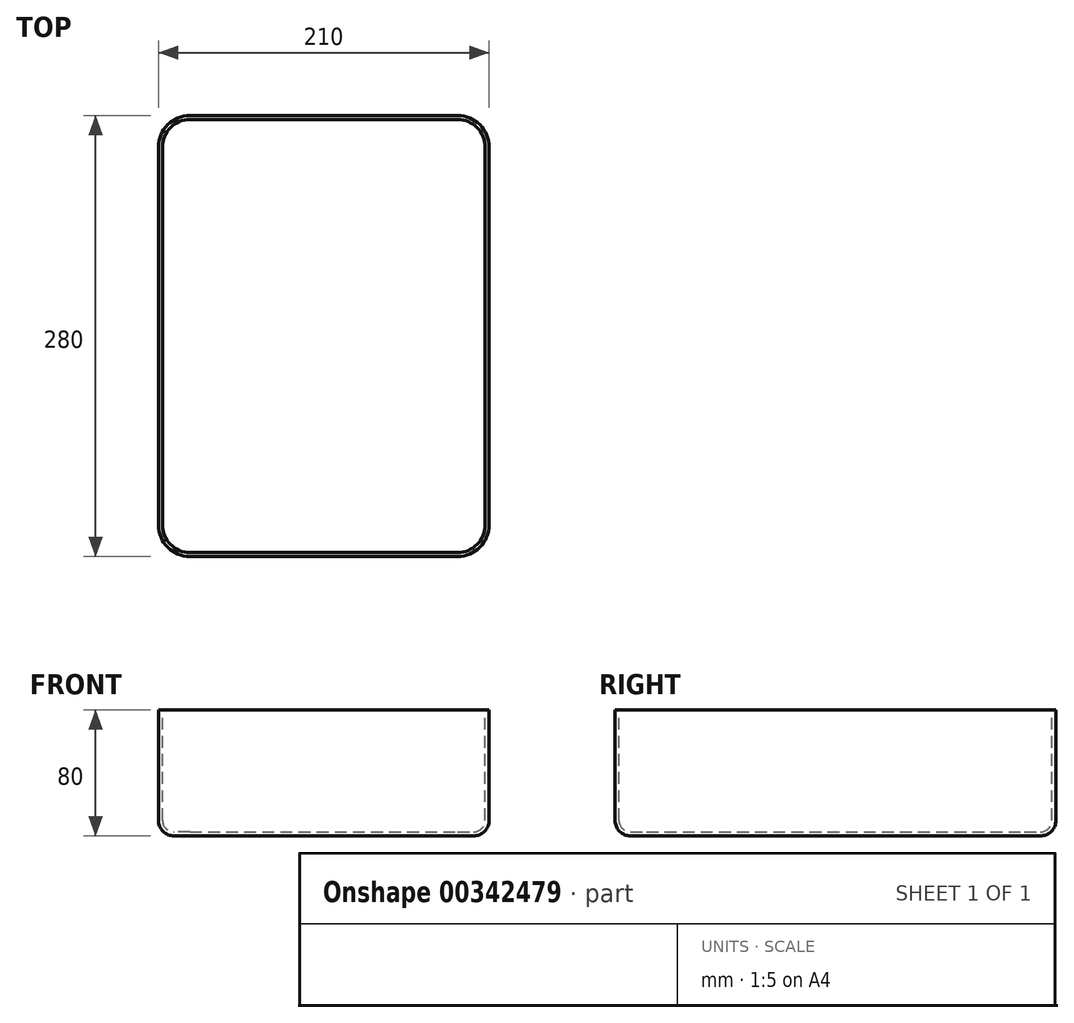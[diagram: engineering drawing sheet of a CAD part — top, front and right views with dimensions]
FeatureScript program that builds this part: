
annotation { "Feature Type Name" : "Feature", "Feature Type Description" : "" }
export const myFeature = defineFeature(function(context is Context, id is Id, definition is map)
    precondition{}
    {
        {
            var Q0;
            Q0=qCreatedBy(makeId("Top.planeOp"),FACE);
            var sketch = newSketch(context, id + "F0", { "sketchPlane" : qUnion([Q0])});
            skLineSegment(sketch, "E0.bottom", {"start": v(0, 0) * mm, "end": v(210, 0) * mm});
            skLineSegment(sketch, "E0.top", {"start": v(0, 280) * mm, "end": v(210, 280) * mm});
            skLineSegment(sketch, "E0.left", {"start": v(0, 0) * mm, "end": v(0, 280) * mm});
            skLineSegment(sketch, "E0.right", {"start": v(210, 0) * mm, "end": v(210, 280) * mm});
            skSolve(sketch);
        }
        {
            var Q0;
            Q0=makeQuery(id+"F0.imprint","IMPRINT",FACE,{"disambiguationData":[TD([[makeQuery(id+"F0.imprint","IMPRINT",EDGE,{"derivedFrom":sQuery(id+"F0.wireOp",EDGE,"E0.bottom")}),1.0]])]});
            extrude(context, id + "F1", {"entities" : qUnion([Q0]), "depth" : 80 * mm});
        }
        {
            var Q0;
            Q0=makeQuery(id+"F1.opExtrude","SWEPT_EDGE",EDGE,{"disambiguationData":[OSD([sQuery(id+"F0.wireOp",EDGE,"E0.top"),sQuery(id+"F0.wireOp",EDGE,"E0.left")])]});
            var Q1;
            Q1=makeQuery(id+"F1.opExtrude","SWEPT_EDGE",EDGE,{"disambiguationData":[OSD([sQuery(id+"F0.wireOp",EDGE,"E0.bottom"),sQuery(id+"F0.wireOp",EDGE,"E0.left")])]});
            var Q2;
            Q2=makeQuery(id+"F1.opExtrude","SWEPT_EDGE",EDGE,{"disambiguationData":[OSD([sQuery(id+"F0.wireOp",EDGE,"E0.bottom"),sQuery(id+"F0.wireOp",EDGE,"E0.right")])]});
            var Q3;
            Q3=makeQuery(id+"F1.opExtrude","SWEPT_EDGE",EDGE,{"disambiguationData":[OSD([sQuery(id+"F0.wireOp",EDGE,"E0.top"),sQuery(id+"F0.wireOp",EDGE,"E0.right")])]});
            fillet(context, id + "F2", {"entities" : qUnion([Q0, Q1, Q2, Q3]), "radius" : 20 * mm, "tangentPropagation" : true, "allowEdgeOverflow" : false});
        }
        {
            var Q0;
            Q0=makeQuery(id+"F1.opExtrude","CAP_EDGE",EDGE,{"disambiguationData":[OSD([sQuery(id+"F0.wireOp",EDGE,"E0.left")])],"isStart":true});
            fillet(context, id + "F3", {"entities" : qUnion([Q0]), "radius" : 10 * mm, "tangentPropagation" : true, "allowEdgeOverflow" : false});
        }
        {
            var Q0;
            Q0=makeQuery(id+"F1.opExtrude","CAP_FACE",FACE,{"disambiguationData":[OSD([sQuery(id+"F0.wireOp",EDGE,"E0.bottom"),sQuery(id+"F0.wireOp",EDGE,"E0.top"),sQuery(id+"F0.wireOp",EDGE,"E0.left"),sQuery(id+"F0.wireOp",EDGE,"E0.right")])],"isStart":false});
            shell(context, id + "F4", {"entities" : qUnion([Q0]), "thickness" : 2.5 * mm});
        }
    });
